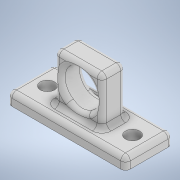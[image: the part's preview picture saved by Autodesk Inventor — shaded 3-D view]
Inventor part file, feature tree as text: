
AUTODESK INVENTOR PART (.ipt)
format: ipt  version: 2021.4 (Build 254397000, 397)  size: 225,792 bytes
history: native  units: mm
features: sketch x4, extrude x2, hole x2, other x1, fillet x1
ambient origin geometry x8: Origin, YZ Plane, XZ Plane, XY Plane, X Axis, Y Axis, Z Axis, Center Point
bodies: Body1 (feature_tree)
feature tree (10):
  other  "ソリッド1"
  extrude  "押し出し1"  Depth=20.0mm
  extrude  "押し出し2"  Depth=50.0mm
  hole  "穴1"  [1 undecoded]
  hole  "穴2"  [1 undecoded]
  fillet  "フィレット1"  Radius=20.0mm
  sketch  "スケッチ1"
  sketch  "スケッチ2"
  sketch  "スケッチ3"
  sketch  "スケッチ4"
note: 2 required parameter values undecoded (feature->parameter linkage not recoverable at this tier; creation-order binding heuristic only, values carry confidence <= 0.55)
